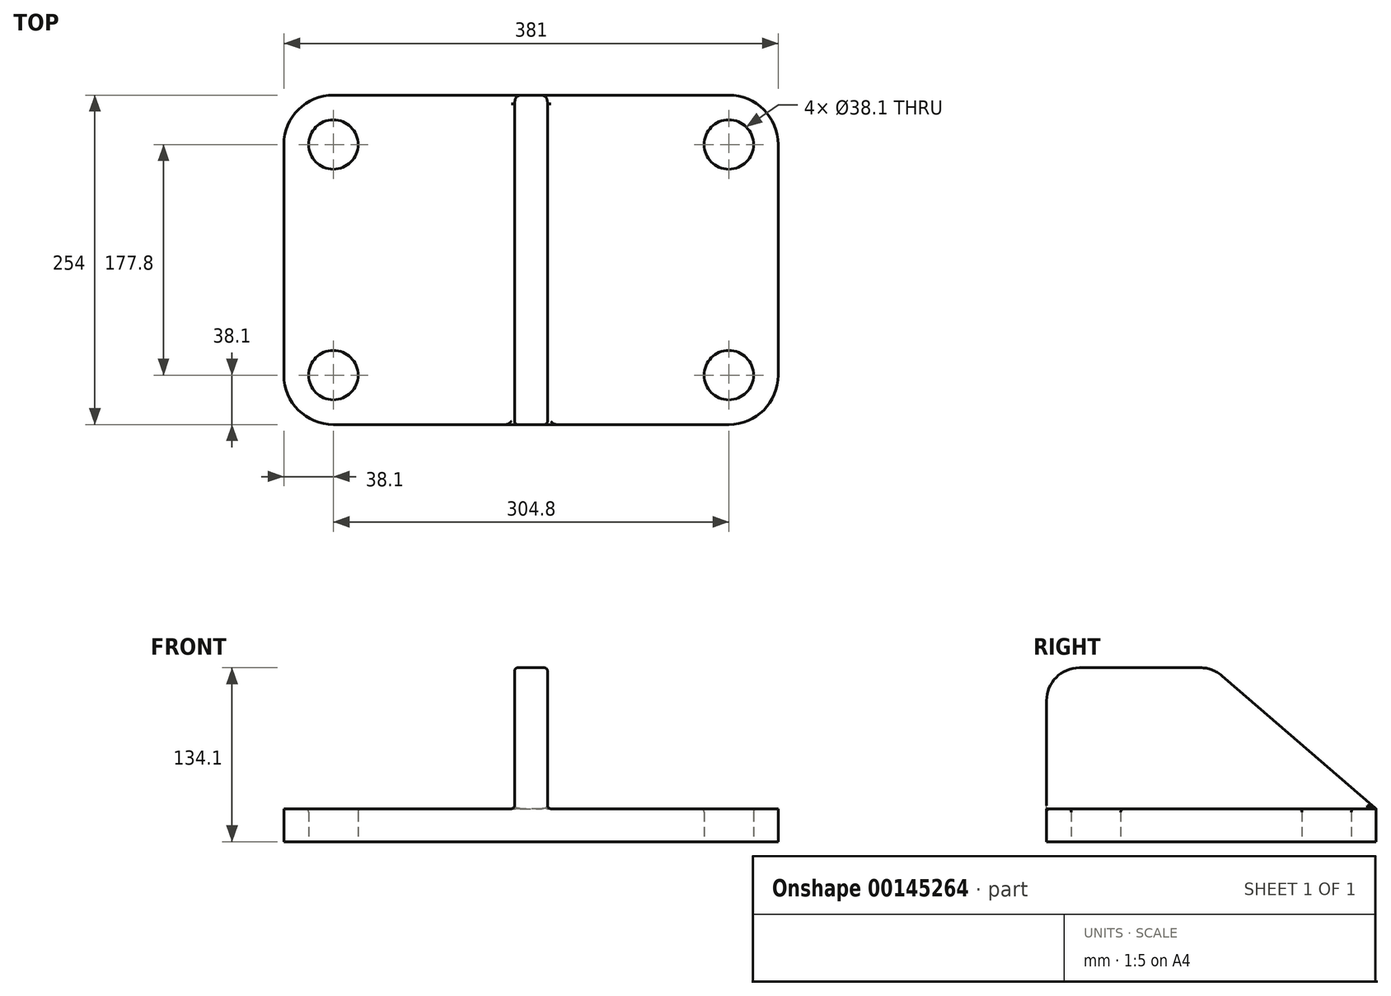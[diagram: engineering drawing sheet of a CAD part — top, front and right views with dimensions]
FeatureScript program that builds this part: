
annotation { "Feature Type Name" : "Feature", "Feature Type Description" : "" }
export const myFeature = defineFeature(function(context is Context, id is Id, definition is map)
    precondition{}
    {
        {
            var Q0;
            Q0=qCreatedBy(makeId("Top.planeOp"),FACE);
            var sketch = newSketch(context, id + "F0", { "sketchPlane" : qUnion([Q0])});
            skLineSegment(sketch, "E0.bottom", {"start": v(0, 0) * mm, "end": v(381, 0) * mm});
            skLineSegment(sketch, "E0.top", {"start": v(0, 254) * mm, "end": v(381, 254) * mm});
            skLineSegment(sketch, "E0.left", {"start": v(0, 0) * mm, "end": v(0, 254) * mm});
            skLineSegment(sketch, "E0.right", {"start": v(381, 0) * mm, "end": v(381, 254) * mm});
            skCircle(sketch, "E1", {"center": v(38.1, 215.9) * mm, "radius": 19.05 * mm});
            skCircle(sketch, "E2.MirrorC", {"center": v(342.9, 215.9) * mm, "radius": 19.05 * mm});
            skCircle(sketch, "E3.MirrorC", {"center": v(342.9, 38.1) * mm, "radius": 19.05 * mm});
            skCircle(sketch, "E4.MirrorC", {"center": v(38.1, 38.1) * mm, "radius": 19.05 * mm});
            skSolve(sketch);
        }
        {
            var Q0;
            Q0=makeQuery(id+"F0.imprint","IMPRINT",FACE,{"disambiguationData":[TD([[makeQuery(id+"F0.imprint","IMPRINT",EDGE,{"derivedFrom":sQuery(id+"F0.wireOp",EDGE,"E0.bottom")}),1.0]])]});
            extrude(context, id + "F1", {"entities" : qUnion([Q0]), "depth" : 25.4 * mm});
        }
        {
            var Q0;
            Q0=qCreatedBy(makeId("Right.planeOp"),FACE);
            cPlane(context, id + "F2", {"entities" : qUnion([Q0]), "cplaneType" : CPlaneType.OFFSET, "offset" : 190.5 * mm, "width" : 152.4 * mm, "height" : 152.4 * mm});
        }
        {
            var Q0;
            Q0=qCreatedBy(id+"F2.planeOp",FACE);
            var sketch = newSketch(context, id + "F3", { "sketchPlane" : qUnion([Q0])});
            skLineSegment(sketch, "E5", {"start": v(0, 25.4) * mm, "end": v(0, 134.1) * mm});
            skLineSegment(sketch, "E6", {"start": v(0, 134.1) * mm, "end": v(127.98, 134.1) * mm});
            skLineSegment(sketch, "E7", {"start": v(127.98, 134.1) * mm, "end": v(253.97, 25.4) * mm});
            skLineSegment(sketch, "E8", {"start": v(253.97, 25.4) * mm, "end": v(0, 25.4) * mm});
            skSolve(sketch);
        }
        {
            var Q0;
            Q0=makeQuery(id+"F3.imprint","IMPRINT",FACE,{"disambiguationData":[TD([[makeQuery(id+"F3.imprint","IMPRINT",EDGE,{"derivedFrom":sQuery(id+"F3.wireOp",EDGE,"E5")}),-1.0]])]});
            extrude(context, id + "F4", {"entities" : qUnion([Q0]), "operationType" : NewBodyOperationType.ADD, "endBound" : BoundingType.SYMMETRIC, "depth" : 25.4 * mm});
        }
        {
            var Q0;
            Q0=makeQuery(id+"F4.opExtrude","SWEPT_EDGE",EDGE,{"disambiguationData":[OSD([sQuery(id+"F3.wireOp",EDGE,"E5"),sQuery(id+"F3.wireOp",EDGE,"E6")])]});
            var Q1;
            Q1=makeQuery(id+"F4.opExtrude","SWEPT_EDGE",EDGE,{"disambiguationData":[OSD([sQuery(id+"F3.wireOp",EDGE,"E6"),sQuery(id+"F3.wireOp",EDGE,"E7")])]});
            fillet(context, id + "F5", {"entities" : qUnion([Q0, Q1]), "radius" : 25.4 * mm, "tangentPropagation" : true, "allowEdgeOverflow" : false});
        }
        {
            var Q0;
            Q0=makeQuery(id+"F4.opExtrude","CAP_FACE",FACE,{"disambiguationData":[OSD([sQuery(id+"F3.wireOp",EDGE,"E5"),sQuery(id+"F3.wireOp",EDGE,"E6"),sQuery(id+"F3.wireOp",EDGE,"E7"),sQuery(id+"F3.wireOp",EDGE,"E8")])],"isStart":false});
            var Q1;
            Q1=makeQuery(id+"F4.opExtrude","CAP_FACE",FACE,{"disambiguationData":[OSD([sQuery(id+"F3.wireOp",EDGE,"E5"),sQuery(id+"F3.wireOp",EDGE,"E6"),sQuery(id+"F3.wireOp",EDGE,"E7"),sQuery(id+"F3.wireOp",EDGE,"E8")])],"isStart":true});
            var Q2;
            Q2=makeQuery(id+"F1.opExtrude","CAP_EDGE",EDGE,{"disambiguationData":[OSD([sQuery(id+"F0.wireOp",EDGE,"E4.MirrorC")])],"isStart":false});
            var Q3;
            Q3=makeQuery(id+"F1.opExtrude","CAP_EDGE",EDGE,{"disambiguationData":[OSD([sQuery(id+"F0.wireOp",EDGE,"E1")])],"isStart":false});
            var Q4;
            Q4=makeQuery(id+"F1.opExtrude","CAP_EDGE",EDGE,{"disambiguationData":[OSD([sQuery(id+"F0.wireOp",EDGE,"E2.MirrorC")])],"isStart":false});
            var Q5;
            Q5=makeQuery(id+"F1.opExtrude","CAP_EDGE",EDGE,{"disambiguationData":[OSD([sQuery(id+"F0.wireOp",EDGE,"E3.MirrorC")])],"isStart":false});
            fillet(context, id + "F6", {"entities" : qUnion([Q0, Q1, Q2, Q3, Q4, Q5]), "radius" : 2.54 * mm, "allowEdgeOverflow" : false});
        }
        {
            var Q0;
            Q0=makeQuery(id+"F1.opExtrude","SWEPT_EDGE",EDGE,{"disambiguationData":[OSD([sQuery(id+"F0.wireOp",EDGE,"E0.bottom"),sQuery(id+"F0.wireOp",EDGE,"E0.left")])]});
            var Q1;
            Q1=makeQuery(id+"F1.opExtrude","SWEPT_EDGE",EDGE,{"disambiguationData":[OSD([sQuery(id+"F0.wireOp",EDGE,"E0.top"),sQuery(id+"F0.wireOp",EDGE,"E0.right")])]});
            var Q2;
            Q2=makeQuery(id+"F1.opExtrude","SWEPT_EDGE",EDGE,{"disambiguationData":[OSD([sQuery(id+"F0.wireOp",EDGE,"E0.bottom"),sQuery(id+"F0.wireOp",EDGE,"E0.right")])]});
            var Q3;
            Q3=makeQuery(id+"F1.opExtrude","SWEPT_EDGE",EDGE,{"disambiguationData":[OSD([sQuery(id+"F0.wireOp",EDGE,"E0.top"),sQuery(id+"F0.wireOp",EDGE,"E0.left")])]});
            fillet(context, id + "F7", {"entities" : qUnion([Q0, Q1, Q2, Q3]), "radius" : 38.1 * mm, "allowEdgeOverflow" : false});
        }
    });
